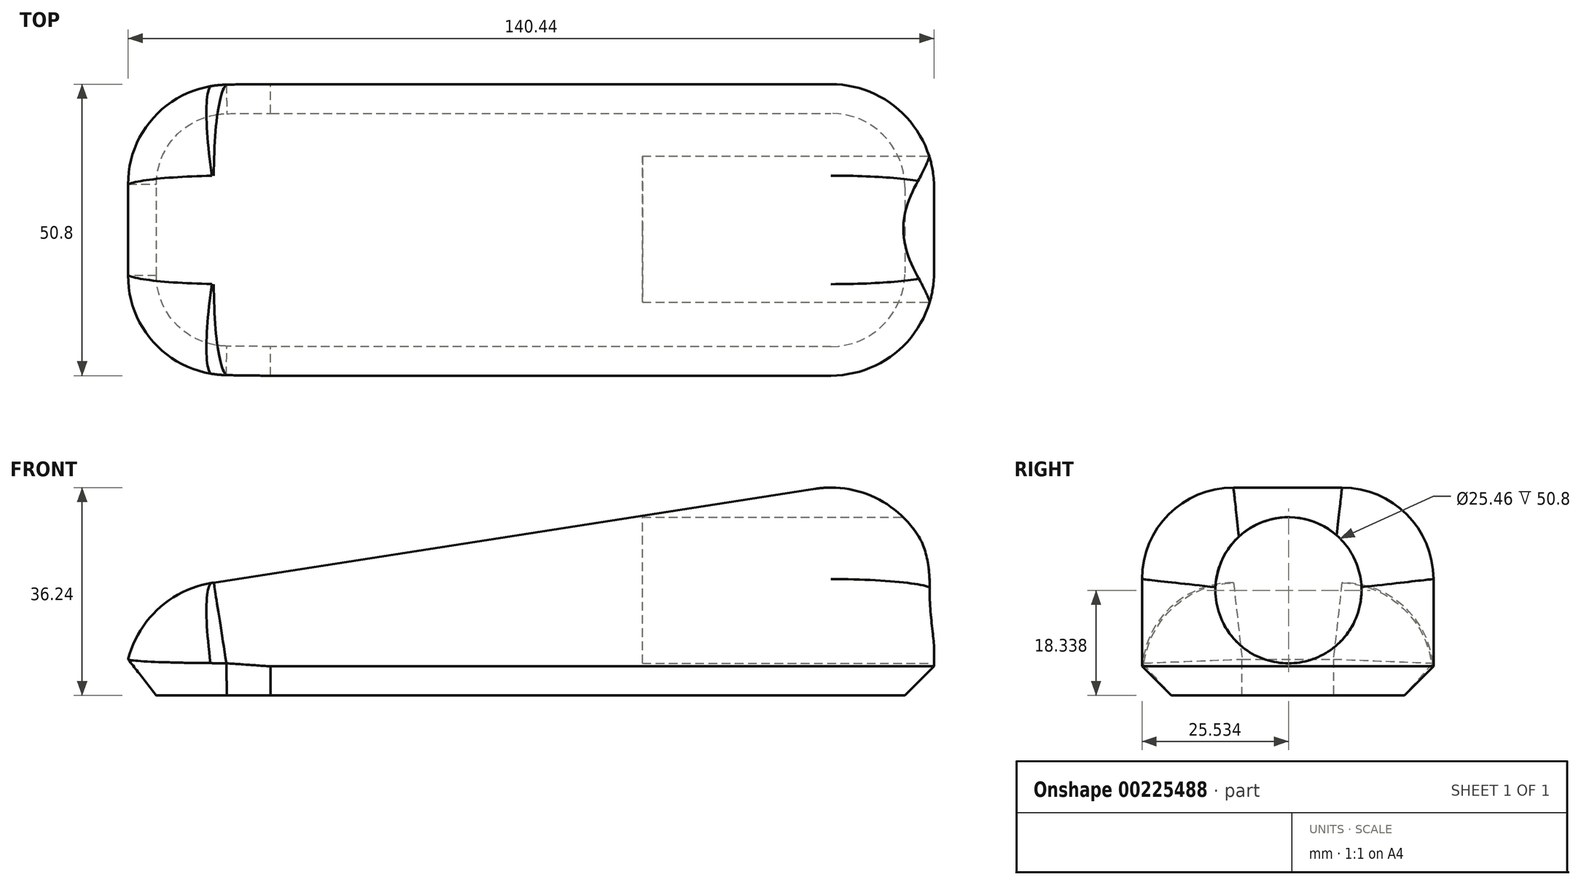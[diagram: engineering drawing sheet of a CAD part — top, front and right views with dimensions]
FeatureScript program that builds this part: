
annotation { "Feature Type Name" : "Feature", "Feature Type Description" : "" }
export const myFeature = defineFeature(function(context is Context, id is Id, definition is map)
    precondition{}
    {
        {
            var Q0;
            Q0=qCreatedBy(makeId("Front.planeOp"),FACE);
            var sketch = newSketch(context, id + "F0", { "sketchPlane" : qUnion([Q0])});
            skLineSegment(sketch, "E0", {"start": v(0, 0) * mm, "end": v(75.8, 0) * mm});
            skLineSegment(sketch, "E1", {"start": v(75.8, 0) * mm, "end": v(75.8, 39.26) * mm});
            skLineSegment(sketch, "E2", {"start": v(75.8, 39.26) * mm, "end": v(-65.2, 17.25) * mm});
            skLineSegment(sketch, "E3", {"start": v(-65.2, 17.25) * mm, "end": v(-65.2, 0) * mm});
            skLineSegment(sketch, "E4", {"start": v(-65.2, 0) * mm, "end": v(0, 0) * mm});
            skSolve(sketch);
        }
        {
            var Q0;
            Q0=makeQuery(id+"F0.imprint","IMPRINT",FACE,{"disambiguationData":[TD([[makeQuery(id+"F0.imprint","IMPRINT",EDGE,{"derivedFrom":sQuery(id+"F0.wireOp",EDGE,"E0")}),1.0]])]});
            extrude(context, id + "F1", {"entities" : qUnion([Q0]), "depth" : 50.8 * mm});
        }
        {
            var Q0;
            Q0=makeQuery(id+"F1.opExtrude","CAP_EDGE",EDGE,{"disambiguationData":[OSD([sQuery(id+"F0.wireOp",EDGE,"E2")])],"isStart":false});
            var Q1;
            Q1=makeQuery(id+"F1.opExtrude","CAP_EDGE",EDGE,{"disambiguationData":[OSD([sQuery(id+"F0.wireOp",EDGE,"E2")])],"isStart":true});
            fillet(context, id + "F2", {"entities" : qUnion([Q0, Q1]), "radius" : 15.94 * mm, "tangentPropagation" : true, "allowEdgeOverflow" : false});
        }
        {
            var Q0;
            Q0=makeQuery(id+"F1.opExtrude","SWEPT_FACE",FACE,{"disambiguationData":[OSD([sQuery(id+"F0.wireOp",EDGE,"E1")])]});
            var sketch = newSketch(context, id + "F3", { "sketchPlane" : qUnion([Q0])});
            skCircle(sketch, "E5", {"center": v(-25.27, 18.34) * mm, "radius": 12.73 * mm});
            skSolve(sketch);
        }
        {
            var Q0;
            Q0 = qSketchRegion(id + "F3", true);
            var Q1;
            Q1=sQuery(id+"F3.wireOp",EDGE,"E5");
            extrude(context, id + "F4", {"entities" : qUnion([Q0]), "operationType" : NewBodyOperationType.REMOVE, "surfaceEntities" : qUnion([Q1]), "oppositeDirection" : true, "depth" : 50.8 * mm});
        }
        {
            var Q0;
            Q0=makeQuery(id+"F1.opExtrude","SWEPT_FACE",FACE,{"disambiguationData":[OSD([sQuery(id+"F0.wireOp",EDGE,"E2")])]});
            fillet(context, id + "F5", {"entities" : qUnion([Q0]), "radius" : 17.95 * mm, "tangentPropagation" : true, "allowEdgeOverflow" : false});
        }
        {
            var Q0;
            Q0=makeQuery(id+"F1.opExtrude","CAP_EDGE",EDGE,{"disambiguationData":[OSD([sQuery(id+"F0.wireOp",EDGE,"E0"),sQuery(id+"F0.wireOp",EDGE,"E4")])],"isStart":false});
            chamfer(context, id + "F6", {"entities" : qUnion([Q0]), "width" : 5.08 * mm, "tangentPropagation" : true});
        }
    });
